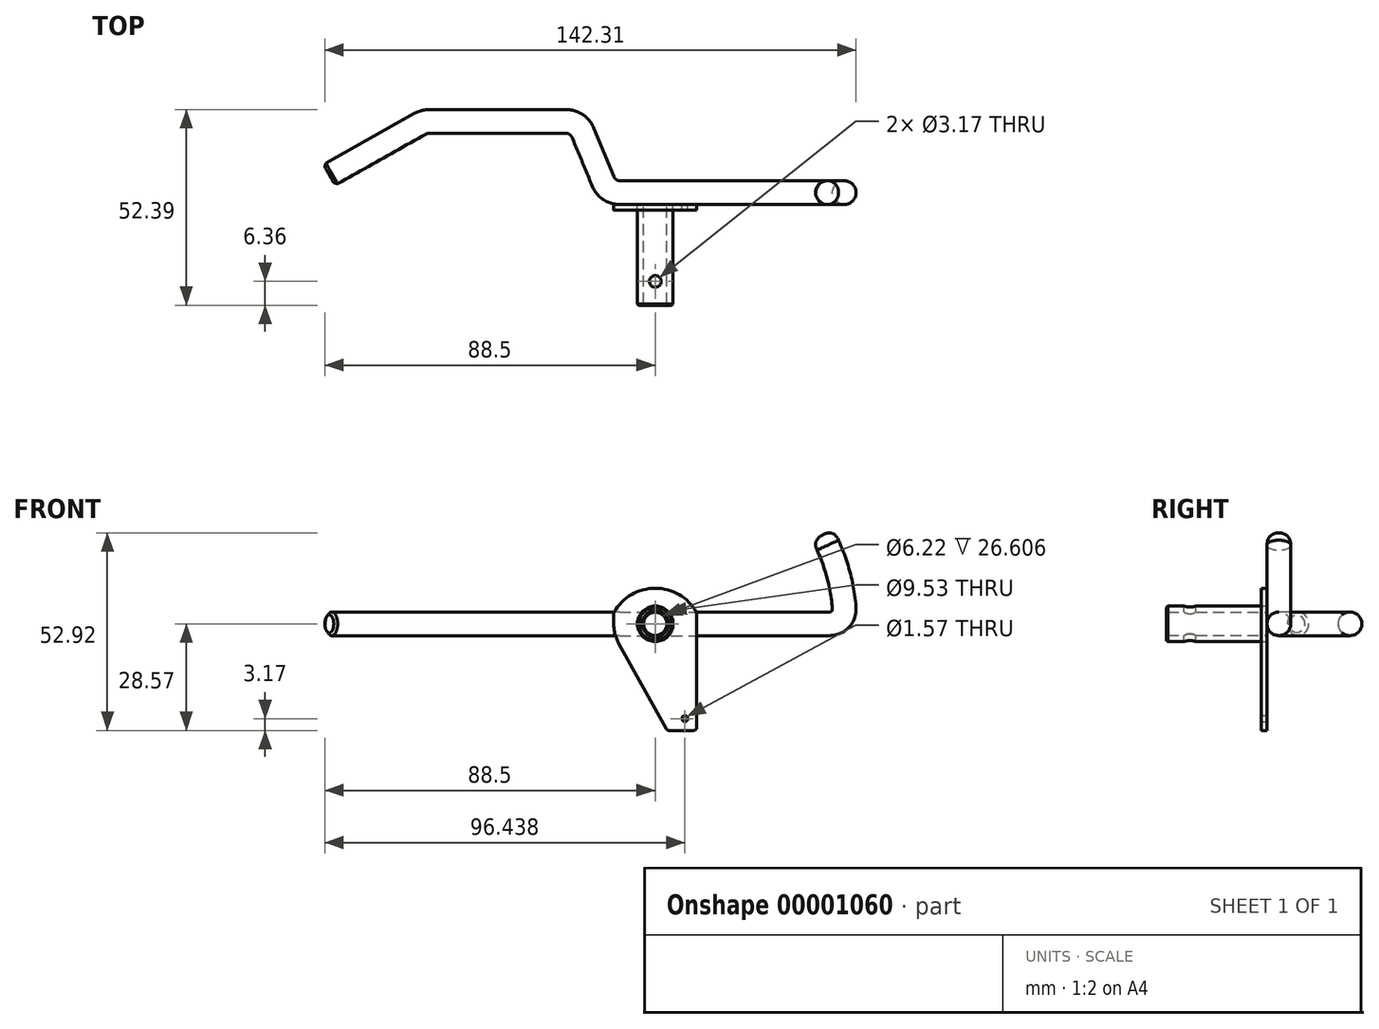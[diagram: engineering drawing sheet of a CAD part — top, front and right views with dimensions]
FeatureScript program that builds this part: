
annotation { "Feature Type Name" : "Feature", "Feature Type Description" : "" }
export const myFeature = defineFeature(function(context is Context, id is Id, definition is map)
    precondition{}
    {
        {
            var Q0;
            Q0=qCreatedBy(makeId("Top.planeOp"),FACE);
            var sketch = newSketch(context, id + "F0", { "sketchPlane" : qUnion([Q0])});
            skLineSegment(sketch, "E0", {"start": v(50.8, 0) * mm, "end": v(-9.53, 0) * mm});
            skLineSegment(sketch, "E1", {"start": v(-13.92, 2.93) * mm, "end": v(-19.42, 16.12) * mm});
            skLineSegment(sketch, "E2", {"start": v(-23.81, 19.05) * mm, "end": v(-60.66, 19.05) * mm});
            skLineSegment(sketch, "E3", {"start": v(-63, 18.44) * mm, "end": v(-87.31, 4.76) * mm});
            skPoint(sketch, "E4.visualSharp", {"position": v(-61.91, 19.05) * mm});
            skArc(sketch, "E4.filletArc", {"start": v(-60.66, 19.05) * mm, "mid": v(-61.87, 18.9) * mm, "end": v(-63, 18.44) * mm});
            skPoint(sketch, "E5.visualSharp", {"position": v(-20.64, 19.05) * mm});
            skArc(sketch, "E5.filletArc", {"start": v(-19.42, 16.12) * mm, "mid": v(-21.17, 18.25) * mm, "end": v(-23.81, 19.05) * mm});
            skPoint(sketch, "E6.visualSharp", {"position": v(-12.7, 0) * mm});
            skArc(sketch, "E6.filletArc", {"start": v(-13.92, 2.93) * mm, "mid": v(-12.17, 0.8) * mm, "end": v(-9.53, 0) * mm});
            skSolve(sketch);
        }
        {
            var Q0;
            Q0=qCreatedBy(makeId("Front.planeOp"),FACE);
            var sketch = newSketch(context, id + "F1", { "sketchPlane" : qUnion([Q0])});
            skArc(sketch, "E7", {"start": v(50.62, 4.3) * mm, "mid": v(48.73, 14.35) * mm, "end": v(44.87, 23.81) * mm});
            skArc(sketch, "E8", {"start": v(46.67, 0) * mm, "mid": v(49.59, 1.28) * mm, "end": v(50.62, 4.3) * mm});
            skPoint(sketch, "E9.orphan", {"position": v(50.8, 0) * mm});
            skSolve(sketch);
        }
        {
            var Q0;
            Q0=sQuery(id+"F0.wireOp",EDGE,"E3");
            var Q1;
            Q1=sQuery(id+"F0.wireOp",VERTEX,"E3.end");
            cPlane(context, id + "F2", {"entities" : qUnion([Q0, Q1]), "cplaneType" : CPlaneType.CURVE_POINT, "offset" : 152.4 * mm, "width" : 152.4 * mm, "height" : 152.4 * mm});
        }
        {
            var Q0;
            Q0=qCreatedBy(id+"F2.planeOp",FACE);
            var sketch = newSketch(context, id + "F3", { "sketchPlane" : qUnion([Q0])});
            skCircle(sketch, "E10", {"center": v(-46.96, 0) * mm, "radius": 3.18 * mm});
            skSolve(sketch);
        }
        {
            var Q0;
            Q0=sQuery(id+"F1.wireOp",EDGE,"E7");
            var Q1;
            Q1=sQuery(id+"F1.wireOp",VERTEX,"E7.end");
            cPlane(context, id + "F4", {"entities" : qUnion([Q0, Q1]), "cplaneType" : CPlaneType.CURVE_POINT, "offset" : 152.4 * mm, "width" : 152.4 * mm, "height" : 152.4 * mm});
        }
        {
            var Q0;
            Q0=qCreatedBy(id+"F4.planeOp",FACE);
            var sketch = newSketch(context, id + "F5", { "sketchPlane" : qUnion([Q0])});
            skCircle(sketch, "E11", {"center": v(50.8, 0) * mm, "radius": 3.18 * mm});
            skSolve(sketch);
        }
        {
            var Q0;
            Q0=makeQuery(id+"F5.imprint","IMPRINT",FACE,{"disambiguationData":[TD([[makeQuery(id+"F5.imprint","IMPRINT",EDGE,{"derivedFrom":sQuery(id+"F5.wireOp",EDGE,"E11")}),1.0]])]});
            var Q1;
            Q1=sQuery(id+"F1.wireOp",EDGE,"E7");
            var Q2;
            Q2=sQuery(id+"F1.wireOp",EDGE,"E8");
            sweep(context, id + "F6", {"profiles" : qUnion([Q0]), "path" : qUnion([Q1, Q2])});
        }
        {
            var Q0;
            Q0=makeQuery(id+"F3.imprint","IMPRINT",FACE,{"disambiguationData":[TD([[makeQuery(id+"F3.imprint","IMPRINT",EDGE,{"derivedFrom":sQuery(id+"F3.wireOp",EDGE,"E10")}),1.0]])]});
            var Q1;
            Q1=sQuery(id+"F0.wireOp",EDGE,"E3");
            var Q2;
            Q2=sQuery(id+"F0.wireOp",EDGE,"E4.filletArc");
            var Q3;
            Q3=sQuery(id+"F0.wireOp",EDGE,"E2");
            var Q4;
            Q4=sQuery(id+"F0.wireOp",EDGE,"E5.filletArc");
            var Q5;
            Q5=sQuery(id+"F0.wireOp",EDGE,"E1");
            var Q6;
            Q6=sQuery(id+"F0.wireOp",EDGE,"E6.filletArc");
            sweep(context, id + "F7", {"profiles" : qUnion([Q0]), "path" : qUnion([Q1, Q2, Q3, Q4, Q5, Q6])});
        }
        {
            var Q0;
            Q0=makeQuery(id+"F6.opSweep","CAP_FACE",FACE,{"disambiguationData":[OSD([sQuery(id+"F1.wireOp",VERTEX,"E8.start"),sQuery(id+"F5.wireOp",EDGE,"E11")])],"isStart":false});
            var Q1;
            Q1=makeQuery(id+"F7.opSweep","CAP_FACE",FACE,{"disambiguationData":[OSD([sQuery(id+"F0.wireOp",VERTEX,"E6.filletArc.end"),sQuery(id+"F3.wireOp",EDGE,"E10")])],"isStart":false});
            extrude(context, id + "F8", {"entities" : qUnion([Q0]), "operationType" : NewBodyOperationType.ADD, "endBound" : BoundingType.UP_TO_BODY, "endBoundEntityBody" : qUnion([Q1]), "depth" : 25.4 * mm});
        }
        {
            var Q0;
            Q0=makeQuery(id+"F7.opSweep","CAP_EDGE",EDGE,{"disambiguationData":[OSD([sQuery(id+"F0.wireOp",VERTEX,"E3.end"),sQuery(id+"F3.wireOp",EDGE,"E10")])],"isStart":true});
            chamfer(context, id + "F9", {"entities" : qUnion([Q0]), "width" : 0.76 * mm, "tangentPropagation" : true});
        }
        {
            var Q0;
            Q0=makeQuery(id+"F6.opSweep","CAP_EDGE",EDGE,{"disambiguationData":[OSD([sQuery(id+"F1.wireOp",VERTEX,"E7.end"),sQuery(id+"F5.wireOp",EDGE,"E11")])],"isStart":true});
            fillet(context, id + "F10", {"entities" : qUnion([Q0]), "radius" : 3.05 * mm, "tangentPropagation" : true, "rho" : 0.5, "crossSection" : FilletCrossSection.CONIC, "allowEdgeOverflow" : false});
        }
        {
            var Q0;
            Q0=qCreatedBy(makeId("Front.planeOp"),FACE);
            cPlane(context, id + "F11", {"entities" : qUnion([Q0]), "cplaneType" : CPlaneType.OFFSET, "offset" : 3.17 * mm, "width" : 152.4 * mm, "height" : 152.4 * mm});
        }
        {
            var Q0;
            Q0=qCreatedBy(id+"F11.planeOp",FACE);
            var sketch = newSketch(context, id + "F12", { "sketchPlane" : qUnion([Q0])});
            skCircle(sketch, "E12", {"center": v(0, 0) * mm, "radius": 4.76 * mm});
            skLineSegment(sketch, "E13.bottom", {"start": v(-11.11, 9.53) * mm, "end": v(11.11, 9.53) * mm});
            skLineSegment(sketch, "E13.top", {"start": v(-11.11, -28.58) * mm, "end": v(11.11, -28.58) * mm});
            skLineSegment(sketch, "E13.left", {"start": v(-11.11, 9.53) * mm, "end": v(-11.11, -28.58) * mm});
            skLineSegment(sketch, "E13.right", {"start": v(11.11, 9.53) * mm, "end": v(11.11, -28.58) * mm});
            skLineSegment(sketch, "E14", {"start": v(0, 0) * mm, "end": v(0, 9.53) * mm, "construction": true});
            skArc(sketch, "E15", {"start": v(11.11, 2.97) * mm, "mid": v(0, 9.52) * mm, "end": v(-11.11, 2.97) * mm});
            skArc(sketch, "E16", {"start": v(-11.11, 0) * mm, "mid": v(-10.76, -2.79) * mm, "end": v(-9.71, -5.4) * mm});
            skLineSegment(sketch, "E17", {"start": v(-9.71, -5.4) * mm, "end": v(3.18, -28.58) * mm});
            skCircle(sketch, "E18", {"center": v(7.94, -25.4) * mm, "radius": 0.79 * mm});
            skSolve(sketch);
        }
        {
            var Q0;
            Q0=makeQuery(id+"F12.imprint","IMPRINT",FACE,{"disambiguationData":[TD([[makeQuery(id+"F12.imprint","IMPRINT",EDGE,{"derivedFrom":sQuery(id+"F12.wireOp",EDGE,"E12")}),-1.0]])]});
            extrude(context, id + "F13", {"entities" : qUnion([Q0]), "operationType" : NewBodyOperationType.ADD, "depth" : 1.57 * mm});
        }
        {
            var Q0;
            Q0=qCreatedBy(id+"F11.planeOp",FACE);
            var sketch = newSketch(context, id + "F14", { "sketchPlane" : qUnion([Q0])});
            skCircle(sketch, "E19.0", {"center": v(0, 0) * mm, "radius": 4.76 * mm});
            skCircle(sketch, "E20", {"center": v(0, 0) * mm, "radius": 3.11 * mm});
            skSolve(sketch);
        }
        {
            var Q0;
            Q0=makeQuery(id+"F14.imprint","IMPRINT",FACE,{"disambiguationData":[TD([[makeQuery(id+"F14.imprint","IMPRINT",EDGE,{"derivedFrom":sQuery(id+"F14.wireOp",EDGE,"E19.0")}),1.0]])]});
            extrude(context, id + "F15", {"entities" : qUnion([Q0]), "depth" : 26.99 * mm});
        }
        {
            var Q0;
            Q0=makeQuery(id+"F13.opExtrude","SWEPT_EDGE",EDGE,{"disambiguationData":[OSD([sQuery(id+"F12.wireOp",EDGE,"E13.right"),sQuery(id+"F12.wireOp",EDGE,"E15")])]});
            var Q1;
            Q1=makeQuery(id+"F13.opExtrude","SWEPT_EDGE",EDGE,{"disambiguationData":[OSD([sQuery(id+"F12.wireOp",EDGE,"E13.top"),sQuery(id+"F12.wireOp",EDGE,"E13.right")])]});
            var Q2;
            Q2=makeQuery(id+"F13.opExtrude","SWEPT_EDGE",EDGE,{"disambiguationData":[OSD([sQuery(id+"F12.wireOp",EDGE,"E13.top"),sQuery(id+"F12.wireOp",EDGE,"E17")])]});
            var Q3;
            Q3=makeQuery(id+"F13.opExtrude","SWEPT_EDGE",EDGE,{"disambiguationData":[OSD([sQuery(id+"F12.wireOp",EDGE,"E13.left"),sQuery(id+"F12.wireOp",EDGE,"E15")])]});
            fillet(context, id + "F16", {"entities" : qUnion([Q0, Q1, Q2, Q3]), "radius" : 0.81 * mm, "tangentPropagation" : true, "allowEdgeOverflow" : false});
        }
        {
            var Q0;
            Q0=makeQuery(id+"F13.opExtrude","CAP_FACE",FACE,{"disambiguationData":[OSD([sQuery(id+"F12.wireOp",EDGE,"E12"),sQuery(id+"F12.wireOp",EDGE,"E13.top"),sQuery(id+"F12.wireOp",EDGE,"E13.left"),sQuery(id+"F12.wireOp",EDGE,"E13.right"),sQuery(id+"F12.wireOp",EDGE,"E15"),sQuery(id+"F12.wireOp",EDGE,"E16"),sQuery(id+"F12.wireOp",EDGE,"E17"),sQuery(id+"F12.wireOp",EDGE,"E18")])],"isStart":false});
            var sketch = newSketch(context, id + "F17", { "sketchPlane" : qUnion([Q0])});
            skPoint(sketch, "E21", {"position": v(0, 0) * mm});
            skSolve(sketch);
        }
        {
            var Q0;
            Q0=qCreatedBy(makeId("Top.planeOp"),FACE);
            var sketch = newSketch(context, id + "F18", { "sketchPlane" : qUnion([Q0])});
            skLineSegment(sketch, "E22", {"start": v(0, -4.75) * mm, "end": v(0, -23.8) * mm, "construction": true});
            skCircle(sketch, "E23", {"center": v(0, -23.8) * mm, "radius": 1.59 * mm});
            skSolve(sketch);
        }
        {
            var Q0;
            Q0=makeQuery(id+"F18.imprint","IMPRINT",FACE,{"disambiguationData":[TD([[makeQuery(id+"F18.imprint","IMPRINT",EDGE,{"derivedFrom":sQuery(id+"F18.wireOp",EDGE,"E23")}),1.0]])]});
            extrude(context, id + "F19", {"entities" : qUnion([Q0]), "operationType" : NewBodyOperationType.REMOVE, "oppositeDirection" : true, "depth" : 12.7 * mm, "symmetric" : true});
        }
        {
            var Q0;
            Q0=makeQuery(id+"F15.opExtrude","CAP_EDGE",EDGE,{"disambiguationData":[OSD([sQuery(id+"F14.wireOp",EDGE,"E19.0")])],"isStart":false});
            var Q1;
            Q1=makeQuery(id+"F15.opExtrude","CAP_EDGE",EDGE,{"disambiguationData":[OSD([sQuery(id+"F14.wireOp",EDGE,"E20")])],"isStart":false});
            chamfer(context, id + "F20", {"entities" : qUnion([Q0, Q1]), "width" : 0.38 * mm, "tangentPropagation" : true});
        }
    });
